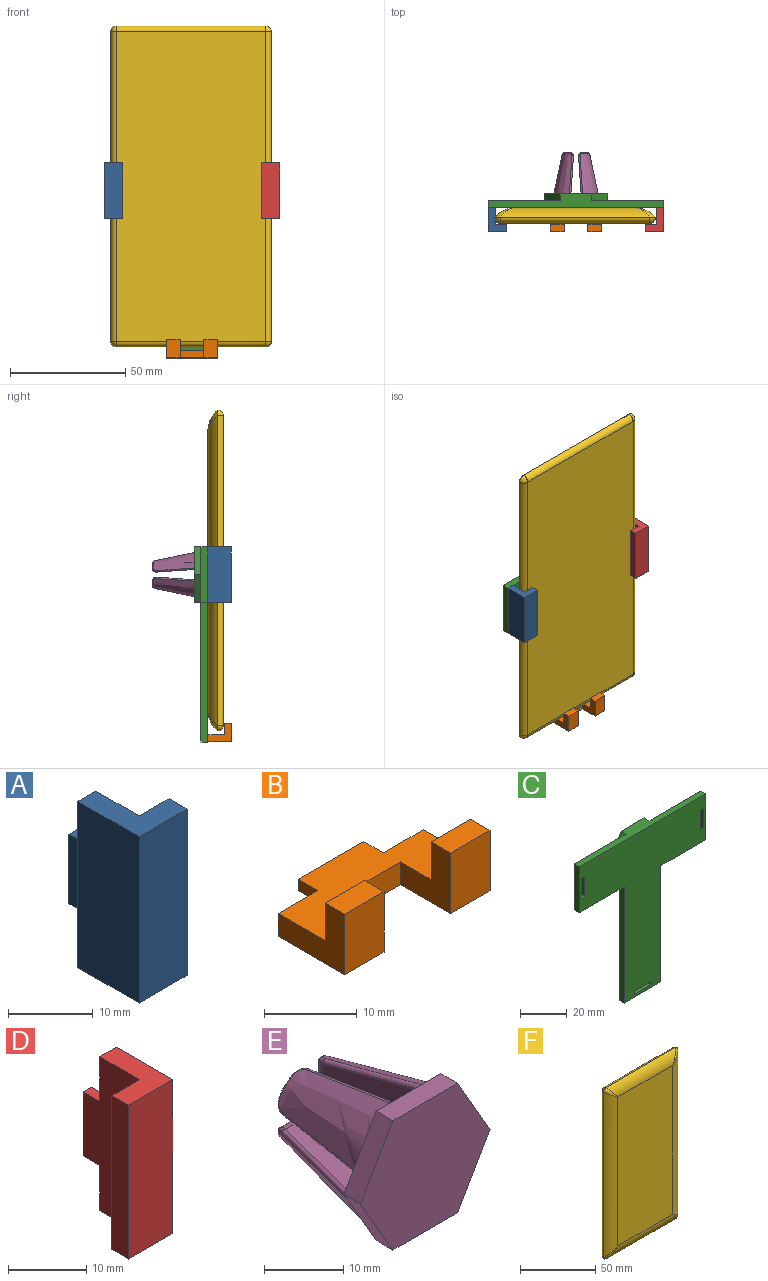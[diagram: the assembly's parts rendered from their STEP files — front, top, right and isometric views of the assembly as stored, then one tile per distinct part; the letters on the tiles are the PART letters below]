
ASSEMBLY  parts=6 mates=5
PART A: 12 faces, bbox 8x13.2x24 mm
  f0: plane 10.2x8mm, normal (0,0,-1), area 45.6mm2, adj f1,f4,f5,f6,f7,f11
  f1: plane 24x10.2mm, normal (1,0,0), area 202.8mm2, adj f0,f2,f3,f7,f8,f10,f11
  f2: plane 10.2x8mm, normal (0,0,1), area 45.6mm2, adj f1,f4,f5,f6,f7,f11
  f3: plane 10x1.5mm, normal (0,1,0), area 15mm2, adj f1,f8,f9,f10
  f4: plane 24x10.2mm, normal (-1,0,0), area 244.8mm2, adj f0,f2,f6,f11
  f5: plane 24x3mm, normal (1,0,0), area 72mm2, adj f0,f2,f6,f7
  f6: plane 24x8mm, normal (0,-1,0), area 192mm2, adj f0,f2,f4,f5
  f7: plane 24x5mm, normal (0,1,0), area 120mm2, adj f0,f1,f2,f5
  f8: plane 3x1.5mm, normal (0,0,1), area 4.5mm2, adj f1,f3,f9,f11
  f9: plane 10x3mm, normal (-1,0,0), area 30mm2, adj f3,f8,f10,f11
  f10: plane 3x1.5mm, normal (0,0,-1), area 4.5mm2, adj f1,f3,f9,f11
  f11: plane 24x3mm, normal (0,1,0), area 57mm2, adj f0,f1,f2,f4,f8,f9,f10
PART B: 18 faces, bbox 22.2x13.2x8 mm
  f0: plane 10x1.5mm, normal (0,1,0), area 15mm2, adj f1,f2,f3,f4
  f1: plane 22.2x10.2mm, normal (0,0,1), area 141.9mm2, adj f0,f3,f4,f5,f6,f7,f9,f12
  f2: plane 10x3mm, normal (0,0,-1), area 30mm2, adj f0,f3,f4,f5
  f3: plane 3x1.5mm, normal (-1,0,0), area 4.5mm2, adj f0,f1,f2,f5
  f4: plane 3x1.5mm, normal (1,0,0), area 4.5mm2, adj f0,f1,f2,f5
  f5: plane 22.2x3mm, normal (0,1,0), area 51.6mm2, adj f1,f2,f3,f4,f7,f8,f16
  f6: plane 8x7.7mm, normal (1,0,0), area 38.1mm2, adj f1,f8,f9,f10,f11,f17
  f7: plane 10.2x8mm, normal (-1,0,0), area 45.6mm2, adj f1,f5,f8,f9,f10,f11
  f8: plane 22.2x10.2mm, normal (0,0,-1), area 147.9mm2, adj f5,f6,f7,f11,f12,f15,f16,f17
  f9: plane 6x5mm, normal (0,1,0), area 30mm2, adj f1,f6,f7,f10
  f10: plane 6x3mm, normal (0,0,1), area 18mm2, adj f6,f7,f9,f11
  f11: plane 8x6mm, normal (0,-1,0), area 48mm2, adj f6,f7,f8,f10
  f12: plane 8x7.7mm, normal (-1,0,0), area 38.1mm2, adj f1,f8,f13,f14,f15,f17
  f13: plane 6x5mm, normal (0,1,0), area 30mm2, adj f1,f12,f14,f16
  f14: plane 6x3mm, normal (0,0,1), area 18mm2, adj f12,f13,f15,f16
  f15: plane 8x6mm, normal (0,-1,0), area 48mm2, adj f8,f12,f14,f16
  f16: plane 10.2x8mm, normal (1,0,0), area 45.6mm2, adj f1,f5,f8,f13,f14,f15
  f17: plane 10.2x3mm, normal (0,-1,0), area 30.6mm2, adj f1,f6,f8,f12
PART C: 35 faces, bbox 76.2x6x84.7 mm
  f0: plane 60.65x3mm, normal (-1,0,0), area 181.9mm2, adj f2,f3,f4,f5
  f1: plane 60.65x3mm, normal (1,0,0), area 181.9mm2, adj f2,f3,f4,f9
  f2: plane 22.2x3mm, normal (0,0,-1), area 66.6mm2, adj f0,f1,f3,f4
  f3: plane 84.65x76.2mm, normal (0,1,0), area 2627.9mm2, adj f0,f1,f2,f5,f6,f7,f8,f9
  f4: plane 84.65x76.2mm, normal (0,-1,0), area 3126.8mm2, adj f0,f1,f2,f5,f6,f7,f8,f9
  f5: plane 27x3mm, normal (0,0,-1), area 81mm2, adj f0,f3,f4,f8
  f6: plane 24x3mm, normal (1,0,0), area 72mm2, adj f3,f4,f7,f9
  f7: plane 76.2x6mm, normal (0,0,1), area 270.2mm2, adj f3,f4,f6,f8,f16,f17,f21
  f8: plane 24x3mm, normal (-1,0,0), area 72mm2, adj f3,f4,f5,f7
  f9: plane 27x3mm, normal (0,0,-1), area 81mm2, adj f1,f3,f4,f6
  f10: plane 10.1x5.83mm, normal (0.87,0,-0.5), area 35mm2, adj f11,f20,f21,f22
  f11: plane 10.1x5.83mm, normal (0.87,0,0.5), area 35mm2, adj f10,f12,f21,f22
  f12: plane 11.66x3mm, normal (0,0,1), area 35mm2, adj f11,f13,f21,f22
  f13: plane 10.1x5.83mm, normal (-0.87,0,0.5), area 35mm2, adj f12,f14,f21,f22
  f14: plane 10.1x5.83mm, normal (-0.87,0,-0.5), area 35mm2, adj f13,f20,f21,f22
  f15: plane 12x6.93mm, normal (-0.87,0,-0.5), area 41.6mm2, adj f3,f16,f19,f21
  f16: plane 12x6.93mm, normal (-0.87,0,0.5), area 41.6mm2, adj f3,f7,f15,f21
  f17: plane 12x6.93mm, normal (0.87,0,0.5), area 41.6mm2, adj f3,f7,f18,f21
  f18: plane 12x6.93mm, normal (0.87,0,-0.5), area 41.6mm2, adj f3,f17,f19,f21
  f19: plane 13.86x3mm, normal (0,0,-1), area 41.6mm2, adj f3,f15,f18,f21
  f20: plane 11.66x3mm, normal (0,0,-1), area 35mm2, adj f10,f14,f21,f22
  f21: plane 27.71x24mm, normal (0,1,0), area 145.5mm2, adj f7,f10,f11,f12,f13,f14,f15,f16
  f22: plane 23.33x20.2mm, normal (0,1,0), area 353.4mm2, adj f10,f11,f12,f13,f14,f20
  f23: plane 10.1x3mm, normal (1,0,0), area 30.3mm2, adj f3,f4,f24,f25
  f24: plane 3x1.6mm, normal (0,0,-1), area 4.8mm2, adj f3,f4,f23,f26
  f25: plane 3x1.6mm, normal (0,0,1), area 4.8mm2, adj f3,f4,f23,f26
  f26: plane 10.1x3mm, normal (-1,0,0), area 30.3mm2, adj f3,f4,f24,f25
  f27: plane 10.1x3mm, normal (0,0,1), area 30.3mm2, adj f3,f4,f28,f29
  f28: plane 3x1.6mm, normal (1,0,0), area 4.8mm2, adj f3,f4,f27,f30
  f29: plane 3x1.6mm, normal (-1,0,0), area 4.8mm2, adj f3,f4,f27,f30
  f30: plane 10.1x3mm, normal (0,0,-1), area 30.3mm2, adj f3,f4,f28,f29
  f31: plane 10.1x3mm, normal (1,0,0), area 30.3mm2, adj f3,f4,f32,f33
  f32: plane 3x1.6mm, normal (0,0,-1), area 4.8mm2, adj f3,f4,f31,f34
  f33: plane 3x1.6mm, normal (0,0,1), area 4.8mm2, adj f3,f4,f31,f34
  f34: plane 10.1x3mm, normal (-1,0,0), area 30.3mm2, adj f3,f4,f32,f33
PART D: 12 faces, bbox 8x13.2x24 mm
  f0: plane 10.2x8mm, normal (0,0,-1), area 45.6mm2, adj f1,f3,f5,f6,f7,f11
  f1: plane 24x10.2mm, normal (1,0,0), area 244.8mm2, adj f0,f4,f6,f11
  f2: plane 10x1.5mm, normal (0,1,0), area 15mm2, adj f3,f8,f9,f10
  f3: plane 24x10.2mm, normal (-1,0,0), area 202.8mm2, adj f0,f2,f4,f7,f8,f10,f11
  f4: plane 10.2x8mm, normal (0,0,1), area 45.6mm2, adj f1,f3,f5,f6,f7,f11
  f5: plane 24x3mm, normal (-1,0,0), area 72mm2, adj f0,f4,f6,f7
  f6: plane 24x8mm, normal (0,-1,0), area 192mm2, adj f0,f1,f4,f5
  f7: plane 24x5mm, normal (0,1,0), area 120mm2, adj f0,f3,f4,f5
  f8: plane 3x1.5mm, normal (0,0,-1), area 4.5mm2, adj f2,f3,f9,f11
  f9: plane 10x3mm, normal (1,0,0), area 30mm2, adj f2,f8,f10,f11
  f10: plane 3x1.5mm, normal (0,0,1), area 4.5mm2, adj f2,f3,f9,f11
  f11: plane 24x3mm, normal (0,1,0), area 57mm2, adj f0,f1,f3,f4,f8,f9,f10
PART E: 60 faces, bbox 23.2x23.4x20.6 mm
  f0: bspline ~17.61x8.12mm, area 143.4mm2, adj f4,f18,f19,f20,f48,f52
  f1: bspline ~17.61x8.12mm, area 143.4mm2, adj f4,f22,f23,f24,f43,f47
  f2: bspline ~17.61x8.12mm, area 143.4mm2, adj f4,f26,f27,f28,f38,f42
  f3: bspline ~17.61x8.12mm, area 143.4mm2, adj f4,f30,f31,f32,f33,f37
  f4: plane 23.15x20.06mm, normal (0,1,0), area 188.5mm2, adj f0,f1,f2,f3,f6,f7,f9,f10
  f5: plane 2.36x2.36mm, normal (0,1,0), area 3.3mm2, adj f31,f34,f36
  f6: plane 16.4x7.48mm, normal (-1,-0.07,0), area 85.4mm2, adj f4,f29,f32,f34
  f7: plane 16.4x7.48mm, normal (0,-0.07,-1), area 85.4mm2, adj f4,f29,f30,f36
  f8: plane 2.36x2.36mm, normal (0,1,0), area 3.3mm2, adj f27,f39,f41
  f9: plane 16.4x7.48mm, normal (1,-0.07,0), area 85.4mm2, adj f4,f25,f28,f39
  f10: plane 16.4x7.48mm, normal (0,-0.07,-1), area 85.4mm2, adj f4,f25,f26,f41
  f11: plane 2.36x2.36mm, normal (0,1,0), area 3.3mm2, adj f23,f44,f46
  f12: plane 16.4x7.48mm, normal (-1,-0.07,0), area 85.4mm2, adj f4,f21,f24,f44
  f13: plane 16.4x7.48mm, normal (0,-0.07,1), area 85.4mm2, adj f4,f21,f22,f46
  f14: plane 2.36x2.36mm, normal (0,1,0), area 3.3mm2, adj f19,f49,f51
  f15: plane 16.4x7.48mm, normal (0,-0.07,1), area 85.4mm2, adj f4,f17,f20,f49
  f16: plane 16.4x7.48mm, normal (1,-0.07,0), area 85.4mm2, adj f4,f17,f18,f51
  f17: cylinder r=0.5mm len=16.41mm, axis (-0.07,-1,-0.07), area 12.9mm2, adj f4,f15,f16,f50
  f18: bspline ~22.72x5.45mm, area 15.7mm2, adj f0,f4,f16,f52
  f19: bspline ~3.89x3.54mm, area 2.4mm2, adj f0,f14,f48,f52
  f20: bspline ~22.72x5.45mm, area 15.7mm2, adj f0,f4,f15,f48
  f21: cylinder r=0.5mm len=16.41mm, axis (0.07,-1,-0.07), area 12.9mm2, adj f4,f12,f13,f45
  f22: bspline ~22.72x5.45mm, area 15.7mm2, adj f1,f4,f13,f47
  f23: bspline ~3.89x3.54mm, area 2.4mm2, adj f1,f11,f43,f47
  f24: bspline ~22.72x5.45mm, area 15.7mm2, adj f1,f4,f12,f43
  f25: cylinder r=0.5mm len=16.41mm, axis (-0.07,-1,0.07), area 12.9mm2, adj f4,f9,f10,f40
  f26: bspline ~22.72x5.45mm, area 15.7mm2, adj f2,f4,f10,f42
  f27: bspline ~3.89x3.54mm, area 2.4mm2, adj f2,f8,f38,f42
  f28: bspline ~22.72x5.45mm, area 15.7mm2, adj f2,f4,f9,f38
  f29: cylinder r=0.5mm len=16.41mm, axis (-0.07,1,-0.07), area 12.9mm2, adj f4,f6,f7,f35
  f30: bspline ~20.18x4.91mm, area 15.7mm2, adj f3,f4,f7,f37
  f31: bspline ~3.62x3.43mm, area 2.4mm2, adj f3,f5,f33,f37
  f32: bspline ~20.18x4.91mm, area 15.7mm2, adj f3,f4,f6,f33
  f33: bspline ~2.03x1.75mm, area 1.9mm2, adj f3,f31,f32,f34
  f34: cylinder r=1.5mm len=4mm, axis (0,0,-1), area 7.8mm2, adj f5,f6,f33,f35
  f35: bspline ~1.76x1.5mm, area 0.9mm2, adj f29,f34,f36
  f36: cylinder r=1.5mm len=4mm, axis (-1,0,0), area 7.8mm2, adj f5,f7,f35,f37
  f37: bspline ~1.99x1.93mm, area 1.9mm2, adj f3,f30,f31,f36
  f38: bspline ~1.99x1.93mm, area 1.9mm2, adj f2,f27,f28,f39
  f39: cylinder r=1.5mm len=4mm, axis (0,0,-1), area 7.8mm2, adj f8,f9,f38,f40
  f40: bspline ~1.76x1.5mm, area 0.9mm2, adj f25,f39,f41
  f41: cylinder r=1.5mm len=4mm, axis (1,0,0), area 7.8mm2, adj f8,f10,f40,f42
  f42: bspline ~2.03x1.75mm, area 1.9mm2, adj f2,f26,f27,f41
  f43: bspline ~1.99x1.93mm, area 1.9mm2, adj f1,f23,f24,f44
  f44: cylinder r=1.5mm len=4mm, axis (0,0,1), area 7.8mm2, adj f11,f12,f43,f45
  f45: bspline ~1.76x1.5mm, area 0.9mm2, adj f21,f44,f46
  f46: cylinder r=1.5mm len=4mm, axis (-1,0,0), area 7.8mm2, adj f11,f13,f45,f47
  f47: bspline ~2.03x1.75mm, area 1.9mm2, adj f1,f22,f23,f46
  f48: bspline ~1.99x1.93mm, area 1.9mm2, adj f0,f19,f20,f49
  f49: cylinder r=1.5mm len=4mm, axis (1,0,0), area 7.8mm2, adj f14,f15,f48,f50
  f50: bspline ~1.76x1.5mm, area 0.9mm2, adj f17,f49,f51
  f51: cylinder r=1.5mm len=4mm, axis (0,0,1), area 7.8mm2, adj f14,f16,f50,f52
  f52: bspline ~2.03x1.75mm, area 1.9mm2, adj f0,f18,f19,f51
  f53: plane 11.55x3mm, normal (0,0,1), area 34.6mm2, adj f4,f54,f58,f59
  f54: plane 10x5.77mm, normal (0.87,0,0.5), area 34.6mm2, adj f4,f53,f55,f59
  f55: plane 10x5.77mm, normal (0.87,0,-0.5), area 34.6mm2, adj f4,f54,f56,f59
  f56: plane 11.55x3mm, normal (0,0,-1), area 34.6mm2, adj f4,f55,f57,f59
  f57: plane 10x5.77mm, normal (-0.87,0,-0.5), area 34.6mm2, adj f4,f56,f58,f59
  f58: plane 10x5.77mm, normal (-0.87,0,0.5), area 34.6mm2, adj f4,f53,f57,f59
  f59: plane 23.09x20mm, normal (0,-1,0), area 346.4mm2, adj f53,f54,f55,f56,f57,f58
PART F: 18 faces, bbox 69.7x6.7x139.3 mm
  f0: plane 121.06x51.46mm, normal (0,-1,0), area 6230mm2, adj f10,f13,f14,f17
  f1: plane 134.3x64.7mm, normal (0,1,0), area 8689.2mm2, adj f3,f4,f7,f8
  f2: sphere r=2.5mm, area 9.8mm2, adj f3,f4,f11
  f3: cylinder r=2.5mm len=64.7mm, axis (-1,0,0), area 254.1mm2, adj f1,f2,f5,f13
  f4: cylinder r=2.5mm len=134.3mm, axis (0,0,-1), area 527.4mm2, adj f1,f2,f6,f10
  f5: sphere r=2.5mm, area 13.4mm2, adj f3,f7,f15
  f6: sphere r=2.5mm, area 9.8mm2, adj f4,f8,f12
  f7: cylinder r=2.5mm len=134.3mm, axis (0,0,1), area 527.4mm2, adj f1,f5,f9,f17
  f8: cylinder r=2.5mm len=64.7mm, axis (1,0,0), area 254.1mm2, adj f1,f6,f9,f14
  f9: sphere r=2.5mm, area 6.2mm2, adj f7,f8,f16
  f10: cylinder r=12mm len=134.3mm, axis (0,0,-1), area 1322.6mm2, adj f0,f4,f11,f12
  f11: bspline ~9.12x9.12mm, area 16.4mm2, adj f2,f10,f13
  f12: bspline ~9.12x9.12mm, area 16.4mm2, adj f6,f10,f14
  f13: cylinder r=12mm len=64.7mm, axis (1,0,0), area 601.6mm2, adj f0,f3,f11,f15
  f14: cylinder r=12mm len=64.7mm, axis (1,0,0), area 601.6mm2, adj f0,f8,f12,f16
  f15: bspline ~9.12x9.12mm, area 16.4mm2, adj f5,f13,f17
  f16: bspline ~9.12x9.12mm, area 16.4mm2, adj f9,f14,f17
  f17: cylinder r=12mm len=134.3mm, axis (0,0,-1), area 1322.6mm2, adj f0,f7,f15,f16
PLACE A t=(-81.2,-40.39,27.55)mm
PLACE B t=(-94.2,-40.39,40.65)mm
PLACE C t=(-94.2,-40.39,27.55)mm
PLACE D t=(-107.2,-40.39,27.55)mm
PLACE E t=(-94.2,-57.39,27.55)mm
PLACE F rot(axis=(1,0,0),180deg) t=(-232.27,-67.09,-8.84)mm
MATE fastened B.f0 <-> C.f3  axis (0,1,0) through (-94.2,-57.39,-42)mm
MATE fastened E.f59 <-> C.f22  axis (0,-1,0) through (-94.2,-57.39,27.55)mm
MATE planar C.f4 <-> F.f0  axis (0,-1,0) through (-94.2,-60.39,9.69)mm
MATE fastened D.f2 <-> C.f3  axis (0,1,0) through (-57.6,-57.39,27.55)mm
MATE fastened A.f3 <-> C.f3  axis (0,1,0) through (-130.8,-57.39,27.55)mm
